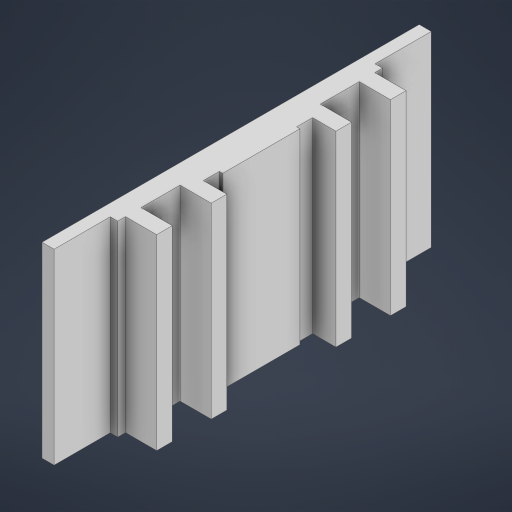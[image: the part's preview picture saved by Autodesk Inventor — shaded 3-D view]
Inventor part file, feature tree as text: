
AUTODESK INVENTOR PART (.ipt)
format: ipt  version: 2024 (Build 280153000, 153)  size: 217,088 bytes
history: native  units: mm
features: extrude x1, mirror x1, sketch x1
ambient origin geometry x8: Origin, YZ Plane, XZ Plane, XY Plane, X Axis, Y Axis, Z Axis, Center Point
bodies: Solid1 (feature_tree)
feature tree (3):
  extrude  "Extrusion1"  Depth=120.0mm TaperAngle=0.0deg
  mirror  "Mirror1"
  sketch  "Sketch1"  dims[d3=5.0mm d5=120.0mm d6=0.0mm d8=10.0mm d9=36.0mm d13=45.0mm d14=24.8mm d15=10.0mm d17=5.0mm d18=2.1mm d19=10.2mm d21=35.0mm]
